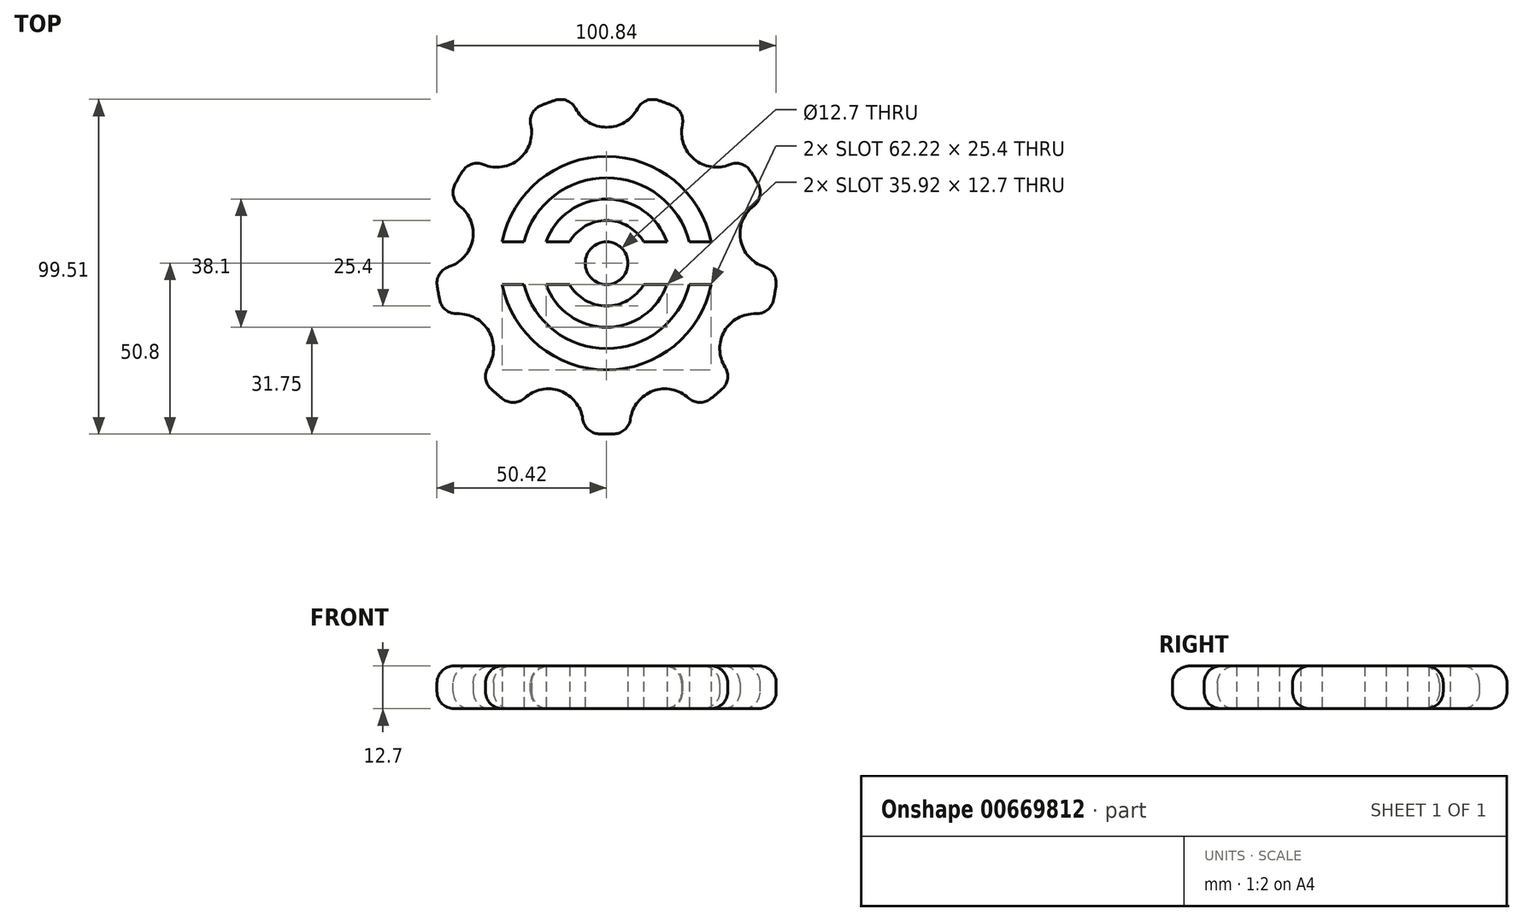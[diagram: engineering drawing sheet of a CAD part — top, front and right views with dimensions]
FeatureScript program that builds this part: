
annotation { "Feature Type Name" : "Feature", "Feature Type Description" : "" }
export const myFeature = defineFeature(function(context is Context, id is Id, definition is map)
    precondition{}
    {
        {
            var Q0;
            Q0=qCreatedBy(makeId("Top.planeOp"),FACE);
            var sketch = newSketch(context, id + "F0", { "sketchPlane" : qUnion([Q0])});
            skArc(sketch, "E0", {"start": v(-50.78, -1.51) * mm, "mid": v(-50.03, -8.82) * mm, "end": v(-48.23, -15.94) * mm});
            skArc(sketch, "E1", {"start": v(-10.3, 49.74) * mm, "mid": v(0, 40.44) * mm, "end": v(10.3, 49.74) * mm});
            skArc(sketch, "E2.1.0", {"start": v(-39.87, 31.48) * mm, "mid": v(-26, 30.98) * mm, "end": v(-24.08, 44.73) * mm});
            skArc(sketch, "E2.2.0", {"start": v(-50.78, -1.51) * mm, "mid": v(-39.82, 7.02) * mm, "end": v(-47.2, 18.8) * mm});
            skArc(sketch, "E2.3.0", {"start": v(-37.92, -33.8) * mm, "mid": v(-35.02, -20.22) * mm, "end": v(-48.23, -15.94) * mm});
            skArc(sketch, "E2.4.0", {"start": v(-7.33, -50.27) * mm, "mid": v(-13.83, -38) * mm, "end": v(-26.7, -43.22) * mm});
            skArc(sketch, "E2.5.0", {"start": v(26.7, -43.22) * mm, "mid": v(13.83, -38) * mm, "end": v(7.33, -50.27) * mm});
            skArc(sketch, "E2.6.0", {"start": v(48.23, -15.94) * mm, "mid": v(35.02, -20.22) * mm, "end": v(37.92, -33.8) * mm});
            skArc(sketch, "E2.7.0", {"start": v(47.2, 18.8) * mm, "mid": v(39.82, 7.02) * mm, "end": v(50.78, -1.51) * mm});
            skArc(sketch, "E2.8.0", {"start": v(24.08, 44.73) * mm, "mid": v(26, 30.98) * mm, "end": v(39.87, 31.48) * mm});
            skArc(sketch, "E3.trimOffspring", {"start": v(-37.92, -33.8) * mm, "mid": v(-32.65, -38.92) * mm, "end": v(-26.7, -43.22) * mm});
            skArc(sketch, "E4.trimOffspring", {"start": v(-7.33, -50.27) * mm, "mid": v(0, -50.8) * mm, "end": v(7.33, -50.27) * mm});
            skArc(sketch, "E5.trimOffspring", {"start": v(26.7, -43.22) * mm, "mid": v(32.65, -38.92) * mm, "end": v(37.92, -33.8) * mm});
            skArc(sketch, "E6.trimOffspring", {"start": v(48.23, -15.94) * mm, "mid": v(50.03, -8.82) * mm, "end": v(50.78, -1.51) * mm});
            skArc(sketch, "E7.trimOffspring", {"start": v(47.2, 18.8) * mm, "mid": v(44, 25.4) * mm, "end": v(39.87, 31.48) * mm});
            skArc(sketch, "E8.trimOffspring", {"start": v(24.08, 44.73) * mm, "mid": v(17.37, 47.74) * mm, "end": v(10.3, 49.74) * mm});
            skArc(sketch, "E9.trimOffspring", {"start": v(-10.3, 49.74) * mm, "mid": v(-17.37, 47.74) * mm, "end": v(-24.08, 44.73) * mm});
            skArc(sketch, "E10.trimOffspring", {"start": v(-39.87, 31.48) * mm, "mid": v(-44, 25.4) * mm, "end": v(-47.2, 18.8) * mm});
            skSolve(sketch);
        }
        {
            var Q0;
            Q0=makeQuery(id+"F0.imprint","IMPRINT",FACE,{"disambiguationData":[TD([[makeQuery(id+"F0.imprint","IMPRINT",EDGE,{"derivedFrom":sQuery(id+"F0.wireOp",EDGE,"E0")}),1.0]])]});
            extrude(context, id + "F1", {"entities" : qUnion([Q0]), "depth" : 12.7 * mm, "offsetDistance" : 25.4 * mm});
        }
        {
            var Q0;
            Q0=makeQuery(id+"F1.opExtrude","CAP_EDGE",EDGE,{"disambiguationData":[OSD([sQuery(id+"F0.wireOp",EDGE,"E10.trimOffspring")])],"isStart":false});
            var Q1;
            Q1=makeQuery(id+"F1.opExtrude","CAP_EDGE",EDGE,{"disambiguationData":[OSD([sQuery(id+"F0.wireOp",EDGE,"E9.trimOffspring")])],"isStart":false});
            var Q2;
            Q2=makeQuery(id+"F1.opExtrude","CAP_EDGE",EDGE,{"disambiguationData":[OSD([sQuery(id+"F0.wireOp",EDGE,"E8.trimOffspring")])],"isStart":false});
            var Q3;
            Q3=makeQuery(id+"F1.opExtrude","CAP_EDGE",EDGE,{"disambiguationData":[OSD([sQuery(id+"F0.wireOp",EDGE,"E7.trimOffspring")])],"isStart":false});
            var Q4;
            Q4=makeQuery(id+"F1.opExtrude","CAP_EDGE",EDGE,{"disambiguationData":[OSD([sQuery(id+"F0.wireOp",EDGE,"E6.trimOffspring")])],"isStart":false});
            var Q5;
            Q5=makeQuery(id+"F1.opExtrude","CAP_EDGE",EDGE,{"disambiguationData":[OSD([sQuery(id+"F0.wireOp",EDGE,"E5.trimOffspring")])],"isStart":false});
            var Q6;
            Q6=makeQuery(id+"F1.opExtrude","CAP_EDGE",EDGE,{"disambiguationData":[OSD([sQuery(id+"F0.wireOp",EDGE,"E4.trimOffspring")])],"isStart":false});
            var Q7;
            Q7=makeQuery(id+"F1.opExtrude","CAP_EDGE",EDGE,{"disambiguationData":[OSD([sQuery(id+"F0.wireOp",EDGE,"E3.trimOffspring")])],"isStart":false});
            var Q8;
            Q8=makeQuery(id+"F1.opExtrude","CAP_EDGE",EDGE,{"disambiguationData":[OSD([sQuery(id+"F0.wireOp",EDGE,"E0")])],"isStart":false});
            fillet(context, id + "F2", {"entities" : qUnion([Q0, Q1, Q2, Q3, Q4, Q5, Q6, Q7, Q8]), "radius" : 5.08 * mm, "tangentPropagation" : true, "allowEdgeOverflow" : false});
        }
        {
            var Q0;
            Q0=makeQuery(id+"F1.opExtrude","CAP_EDGE",EDGE,{"disambiguationData":[OSD([sQuery(id+"F0.wireOp",EDGE,"E9.trimOffspring")])],"isStart":true});
            var Q1;
            Q1=makeQuery(id+"F1.opExtrude","CAP_EDGE",EDGE,{"disambiguationData":[OSD([sQuery(id+"F0.wireOp",EDGE,"E8.trimOffspring")])],"isStart":true});
            var Q2;
            Q2=makeQuery(id+"F1.opExtrude","CAP_EDGE",EDGE,{"disambiguationData":[OSD([sQuery(id+"F0.wireOp",EDGE,"E7.trimOffspring")])],"isStart":true});
            var Q3;
            Q3=makeQuery(id+"F1.opExtrude","CAP_EDGE",EDGE,{"disambiguationData":[OSD([sQuery(id+"F0.wireOp",EDGE,"E6.trimOffspring")])],"isStart":true});
            var Q4;
            Q4=makeQuery(id+"F1.opExtrude","CAP_EDGE",EDGE,{"disambiguationData":[OSD([sQuery(id+"F0.wireOp",EDGE,"E5.trimOffspring")])],"isStart":true});
            var Q5;
            Q5=makeQuery(id+"F1.opExtrude","CAP_EDGE",EDGE,{"disambiguationData":[OSD([sQuery(id+"F0.wireOp",EDGE,"E4.trimOffspring")])],"isStart":true});
            var Q6;
            Q6=makeQuery(id+"F1.opExtrude","CAP_EDGE",EDGE,{"disambiguationData":[OSD([sQuery(id+"F0.wireOp",EDGE,"E3.trimOffspring")])],"isStart":true});
            var Q7;
            Q7=makeQuery(id+"F1.opExtrude","CAP_EDGE",EDGE,{"disambiguationData":[OSD([sQuery(id+"F0.wireOp",EDGE,"E0")])],"isStart":true});
            var Q8;
            Q8=makeQuery(id+"F1.opExtrude","CAP_EDGE",EDGE,{"disambiguationData":[OSD([sQuery(id+"F0.wireOp",EDGE,"E10.trimOffspring")])],"isStart":true});
            fillet(context, id + "F3", {"entities" : qUnion([Q0, Q1, Q2, Q3, Q4, Q5, Q6, Q7, Q8]), "radius" : 5.08 * mm, "tangentPropagation" : true, "allowEdgeOverflow" : false});
        }
        {
            var Q0;
            Q0=makeQuery(id+"F1.opExtrude","CAP_EDGE",EDGE,{"disambiguationData":[OSD([sQuery(id+"F0.wireOp",EDGE,"E1")])],"isStart":true});
            var Q1;
            Q1=makeQuery(id+"F1.opExtrude","CAP_EDGE",EDGE,{"disambiguationData":[OSD([sQuery(id+"F0.wireOp",EDGE,"E2.8.0")])],"isStart":true});
            var Q2;
            Q2=makeQuery(id+"F1.opExtrude","CAP_EDGE",EDGE,{"disambiguationData":[OSD([sQuery(id+"F0.wireOp",EDGE,"E2.7.0")])],"isStart":false});
            var Q3;
            Q3=makeQuery(id+"F1.opExtrude","CAP_EDGE",EDGE,{"disambiguationData":[OSD([sQuery(id+"F0.wireOp",EDGE,"E2.6.0")])],"isStart":false});
            var Q4;
            Q4=makeQuery(id+"F1.opExtrude","CAP_EDGE",EDGE,{"disambiguationData":[OSD([sQuery(id+"F0.wireOp",EDGE,"E2.5.0")])],"isStart":false});
            var Q5;
            Q5=makeQuery(id+"F1.opExtrude","CAP_EDGE",EDGE,{"disambiguationData":[OSD([sQuery(id+"F0.wireOp",EDGE,"E2.4.0")])],"isStart":false});
            var Q6;
            Q6=makeQuery(id+"F1.opExtrude","CAP_EDGE",EDGE,{"disambiguationData":[OSD([sQuery(id+"F0.wireOp",EDGE,"E2.3.0")])],"isStart":false});
            var Q7;
            Q7=makeQuery(id+"F1.opExtrude","CAP_EDGE",EDGE,{"disambiguationData":[OSD([sQuery(id+"F0.wireOp",EDGE,"E2.2.0")])],"isStart":false});
            var Q8;
            Q8=makeQuery(id+"F1.opExtrude","CAP_EDGE",EDGE,{"disambiguationData":[OSD([sQuery(id+"F0.wireOp",EDGE,"E2.1.0")])],"isStart":false});
            fillet(context, id + "F4", {"entities" : qUnion([Q0, Q1, Q2, Q3, Q4, Q5, Q6, Q7, Q8]), "radius" : 5.08 * mm, "tangentPropagation" : true, "allowEdgeOverflow" : false});
        }
        {
            var Q0;
            Q0=qCreatedBy(makeId("Top.planeOp"),FACE);
            var sketch = newSketch(context, id + "F5", { "sketchPlane" : qUnion([Q0])});
            skCircle(sketch, "E11", {"center": v(0, 0) * mm, "radius": 31.75 * mm});
            skCircle(sketch, "E12", {"center": v(0, 0) * mm, "radius": 25.4 * mm});
            skSolve(sketch);
        }
        {
            var Q0;
            Q0=qCreatedBy(makeId("Top.planeOp"),FACE);
            var sketch = newSketch(context, id + "F6", { "sketchPlane" : qUnion([Q0])});
            skCircle(sketch, "E13", {"center": v(0, 0) * mm, "radius": 19.05 * mm});
            skCircle(sketch, "E14", {"center": v(0, 0) * mm, "radius": 12.7 * mm});
            skSolve(sketch);
        }
        {
            var Q0;
            Q0=qCreatedBy(makeId("Top.planeOp"),FACE);
            var sketch = newSketch(context, id + "F7", { "sketchPlane" : qUnion([Q0])});
            skCircle(sketch, "E15", {"center": v(0, 0) * mm, "radius": 6.35 * mm});
            skSolve(sketch);
        }
        {
            var Q0;
            Q0 = qSketchRegion(id + "F5", true);
            extrude(context, id + "F8", {"entities" : qUnion([Q0]), "operationType" : NewBodyOperationType.REMOVE, "oppositeDirection" : true, "depth" : -25.4 * mm, "offsetDistance" : 25.4 * mm});
        }
        {
            var Q0;
            Q0 = qSketchRegion(id + "F6", true);
            extrude(context, id + "F9", {"entities" : qUnion([Q0]), "operationType" : NewBodyOperationType.REMOVE, "depth" : 59.94 * mm, "offsetDistance" : 25.4 * mm});
        }
        {
            var Q0;
            Q0 = qSketchRegion(id + "F7", true);
            extrude(context, id + "F10", {"entities" : qUnion([Q0]), "operationType" : NewBodyOperationType.REMOVE, "depth" : 44.45 * mm, "offsetDistance" : 25.4 * mm});
        }
        {
            var Q0;
            Q0=qCreatedBy(makeId("Top.planeOp"),FACE);
            var sketch = newSketch(context, id + "F11", { "sketchPlane" : qUnion([Q0])});
            skLineSegment(sketch, "E16.bottom", {"start": v(-33.84, 6.35) * mm, "end": v(-7.07, 6.35) * mm});
            skLineSegment(sketch, "E16.top", {"start": v(-33.84, -6.35) * mm, "end": v(-7.07, -6.35) * mm});
            skLineSegment(sketch, "E16.left", {"start": v(-33.84, 6.35) * mm, "end": v(-33.84, -6.35) * mm});
            skLineSegment(sketch, "E16.right", {"start": v(-7.07, 6.35) * mm, "end": v(-7.07, -6.35) * mm});
            skLineSegment(sketch, "E17.bottom", {"start": v(9.78, 6.35) * mm, "end": v(35.04, 6.35) * mm});
            skLineSegment(sketch, "E17.top", {"start": v(9.78, -6.35) * mm, "end": v(35.04, -6.35) * mm});
            skLineSegment(sketch, "E17.left", {"start": v(9.78, 6.35) * mm, "end": v(9.78, -6.35) * mm});
            skLineSegment(sketch, "E17.right", {"start": v(35.04, 6.35) * mm, "end": v(35.04, -6.35) * mm});
            skSolve(sketch);
        }
        {
            var Q0;
            Q0 = qSketchRegion(id + "F11", true);
            extrude(context, id + "F12", {"entities" : qUnion([Q0]), "operationType" : NewBodyOperationType.ADD, "depth" : 12.7 * mm, "offsetDistance" : 25.4 * mm});
        }
    });
